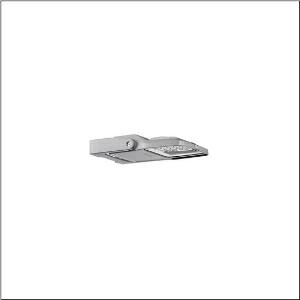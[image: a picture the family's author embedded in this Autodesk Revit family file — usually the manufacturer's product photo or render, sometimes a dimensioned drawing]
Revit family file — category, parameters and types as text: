
# Revit family: floodlight_fl_21_iq_micro___pl64_5xa7762a4e2a_da81
name_source: partatom
category: Lighting Fixtures
units: mm (PartAtom-declared; Revit-internal decimal feet)

## family parameters
Cut with Voids When Loaded = No
Host = Face
Light Source = No
Part Type = Normal
Room Calculation Point = No
Round Connector Dimension = Use Diameter
Shared = No

## types (1)
- --- (1 x LED, 2980 lm, 23.1 W, 4000K)
    Apparent Load = 23 VA
    CIE Flux Codes = 28 80 98 100 100
    Color Rendering = 70
    Color Temperature = 4000K
    Default Elevation = 1800 mm
    Description = Floodlight FL 21 iQ micro, floodlight, primary light control with lens, of PMMA, primary optical cover: protective disc, of toughened safety glass, transparent, light distribution: PL64, light emission: direct distribution, installation type: surface-mounted, LED, High Power LED, rated luminous flux: 2.980lm, luminous efficacy: 129lm/W, light colour: 740, colour temperature: 4000K, control: Auto-Match, Temp-Guard, Night-Set, Smart-Wire, Desk-Remote (wireless, voltage-free reading and setting of iQ features in the workshop via application-optimized NFC function/RFID function), optimised constant luminous flux control (CLO 2.0), Street-Remote, with terminal, 6-pole, mains connection: 220..240V, AC, 50/60Hz, start of lifetime: 23W, end of service life: 24W, reduction: 11W, luminaire housing, of diecast aluminium, powder-coated, Siteco® metallic grey (DB 702S), corrosivity category C5 mid according to DIN EN ISO 12944, sealing non-destructively replaceable, design bracket, of diecast aluminium, powder-coated, Siteco® metallic grey (DB 702S), protection rating (complete): IP66, insulation class (complete): insulation class II (safety insulation), certification: CE, ENEC, VDE, protection symbol: D, impact resistance: IK07, permissible operating ambient temperature: -40..+40°C, permissible operating ambient temperature for outdoor applications: -40..+50°C, standard: DIN EN 12944, LABS conformity tested according to VDMA 24364:2018-05, packaging unit: 1 piece

Light Distribution: PL64
    Height = 65 mm
    Lamp = 1 x LED
    Lamp Light Flux = 2980 lm
    Lamp Power = 23.1 W
    Lamp count = 1
    Length = 312 mm
    Luminous efficacy = 129 lm/W
    Manufacturer = Siteco
    ModVariant = No
    Model = 5XA7762A4E2A
    Mounting Place = Wall
    Mounting Type = Surface mounted
    Number of Poles = 1
    OnlyDefault = Yes
    Power Factor = 1
    Product Name = Floodlight FL 21 iQ micro | PL64
    Product group = floodlight | wall mounted
    ProductGroupID = 2001
    Protection Class = Protection class II
    Protection Degree = IP 66
    RLX_Detail_Level = 1
    RLX_Emergency_Light_Flux = 0 lm
    RLX_Emergency_Type = 0
    RLX_Emergency_Type_DB = No
    RlxData = <blob elided: 97345 chars, md5=ecf215b2>
    Socket = socket
    Standby Power = 0 W
    System Light Flux = 2980 lm
    System Power = 23 W
    Type Comments = factory setting: luminous flux: 100 % | dim-lin: 254 | 455 mA
    Type Image = l_1006878.jpg
    URL = http://relux.com
    VarID = @adj_152043
    Voltage = 0 V
    Weight = 0.00 kg
    Width = 230 mm

## geometry (parser evidence)
native form markers: Blend x4, Sweep x14
no freeform markers — native parametric forms only
